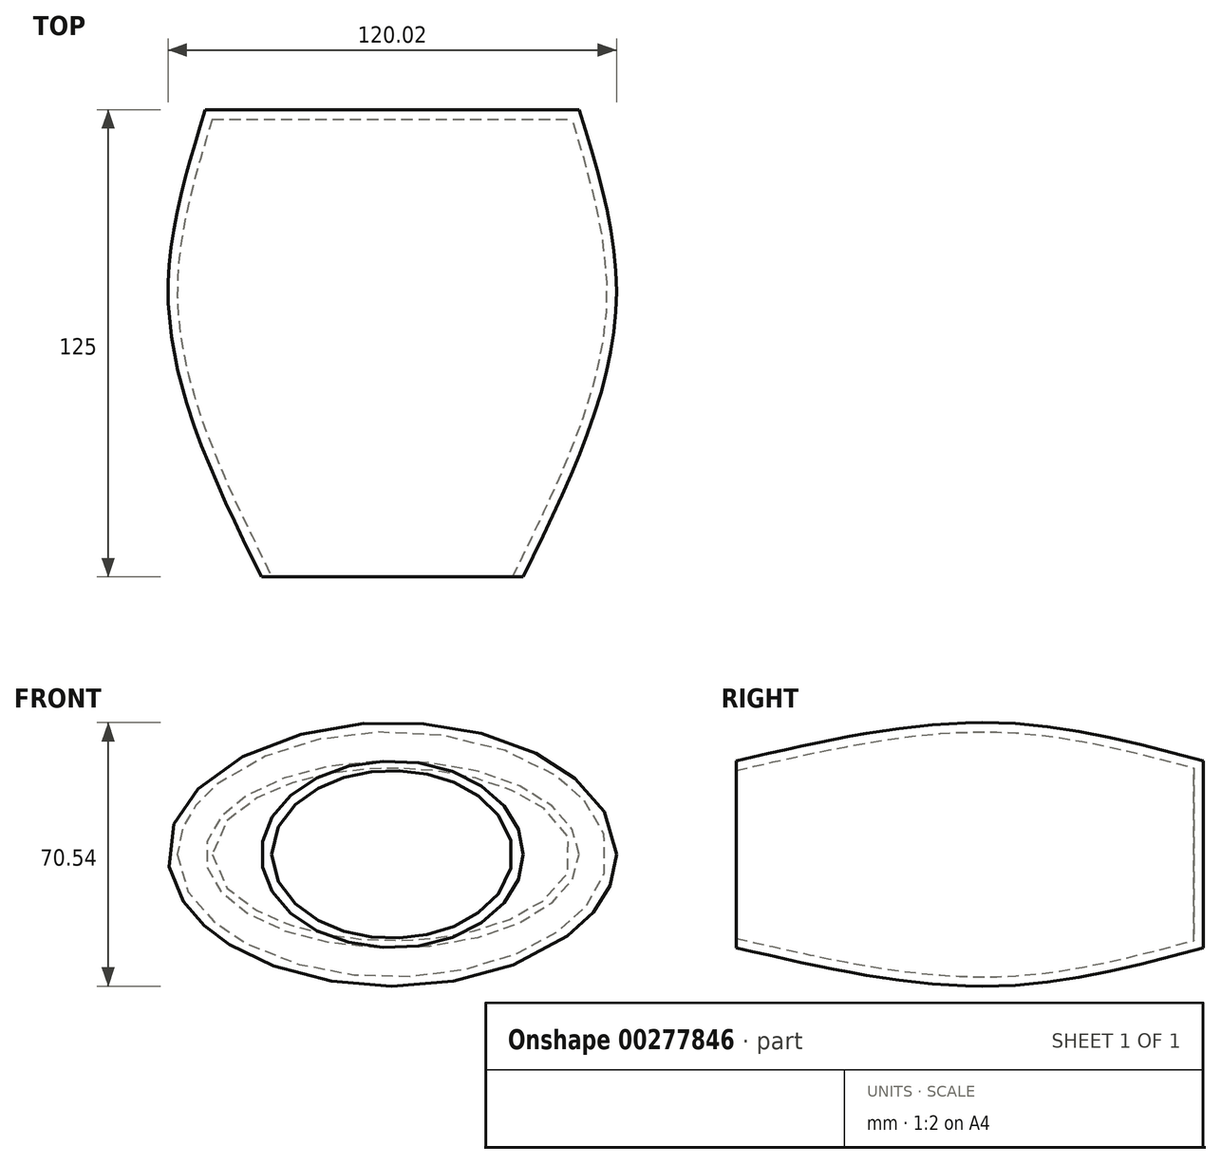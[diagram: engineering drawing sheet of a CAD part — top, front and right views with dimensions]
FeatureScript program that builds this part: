
annotation { "Feature Type Name" : "Feature", "Feature Type Description" : "" }
export const myFeature = defineFeature(function(context is Context, id is Id, definition is map)
    precondition{}
    {
        {
            var Q0;
            Q0=qCreatedBy(makeId("Front.planeOp"),FACE);
            var sketch = newSketch(context, id + "F0", { "sketchPlane" : qUnion([Q0])});
            skEllipse(sketch, "E0", {"center": v(0, 0) * mm, "majorRadius": 50 * mm, "minorRadius": 25 * mm, "majorAxis": v(1, 0)});
            skSolve(sketch);
        }
        {
            var Q0;
            Q0=qCreatedBy(makeId("Front.planeOp"),FACE);
            cPlane(context, id + "F1", {"entities" : qUnion([Q0]), "cplaneType" : CPlaneType.OFFSET, "offset" : 50 * mm, "width" : 150 * mm, "height" : 150 * mm});
        }
        {
            var Q0;
            Q0=qCreatedBy(id+"F1.planeOp",FACE);
            var sketch = newSketch(context, id + "F2", { "sketchPlane" : qUnion([Q0])});
            skEllipse(sketch, "E1", {"center": v(0, 0) * mm, "majorRadius": 60 * mm, "minorRadius": 35 * mm, "majorAxis": v(1, 0)});
            skSolve(sketch);
        }
        {
            var Q0;
            Q0=qCreatedBy(id+"F1.planeOp",FACE);
            cPlane(context, id + "F3", {"entities" : qUnion([Q0]), "cplaneType" : CPlaneType.OFFSET, "offset" : 75 * mm, "width" : 150 * mm, "height" : 150 * mm});
        }
        {
            var Q0;
            Q0=qCreatedBy(id+"F3.planeOp",FACE);
            var sketch = newSketch(context, id + "F4", { "sketchPlane" : qUnion([Q0])});
            skEllipse(sketch, "E2", {"center": v(0, 0) * mm, "majorRadius": 25 * mm, "minorRadius": 35 * mm, "majorAxis": v(0, 1)});
            skSolve(sketch);
        }
        {
            var Q0;
            Q0=makeQuery(id+"F0.imprint","IMPRINT",FACE,{"disambiguationData":[TD([[makeQuery(id+"F0.imprint","IMPRINT",EDGE,{"derivedFrom":sQuery(id+"F0.wireOp",EDGE,"E0")}),1.0]])]});
            var Q1;
            Q1=makeQuery(id+"F2.imprint","IMPRINT",FACE,{"disambiguationData":[TD([[makeQuery(id+"F2.imprint","IMPRINT",EDGE,{"derivedFrom":sQuery(id+"F2.wireOp",EDGE,"E1")}),1.0]])]});
            var Q2;
            Q2=makeQuery(id+"F4.imprint","IMPRINT",FACE,{"disambiguationData":[TD([[makeQuery(id+"F4.imprint","IMPRINT",EDGE,{"derivedFrom":sQuery(id+"F4.wireOp",EDGE,"E2")}),1.0]])]});
            loft(context, id + "F5", {"sheetProfilesArray" : [{ "sheetProfileEntities" : qUnion([Q0]) }, { "sheetProfileEntities" : qUnion([Q1]) }, { "sheetProfileEntities" : qUnion([Q2]) }]});
        }
        {
            var Q0;
            Q0=makeQuery(id+"F5.opLoft","CAP_FACE",FACE,{"disambiguationData":[OSD([makeQuery(id+"F4.imprint","IMPRINT",FACE,{"disambiguationData":[TD([[makeQuery(id+"F4.imprint","IMPRINT",EDGE,{"derivedFrom":sQuery(id+"F4.wireOp",EDGE,"E2")}),1.0]])]})])],"isStart":true});
            shell(context, id + "F6", {"entities" : qUnion([Q0]), "thickness" : 2.5 * mm});
        }
    });
